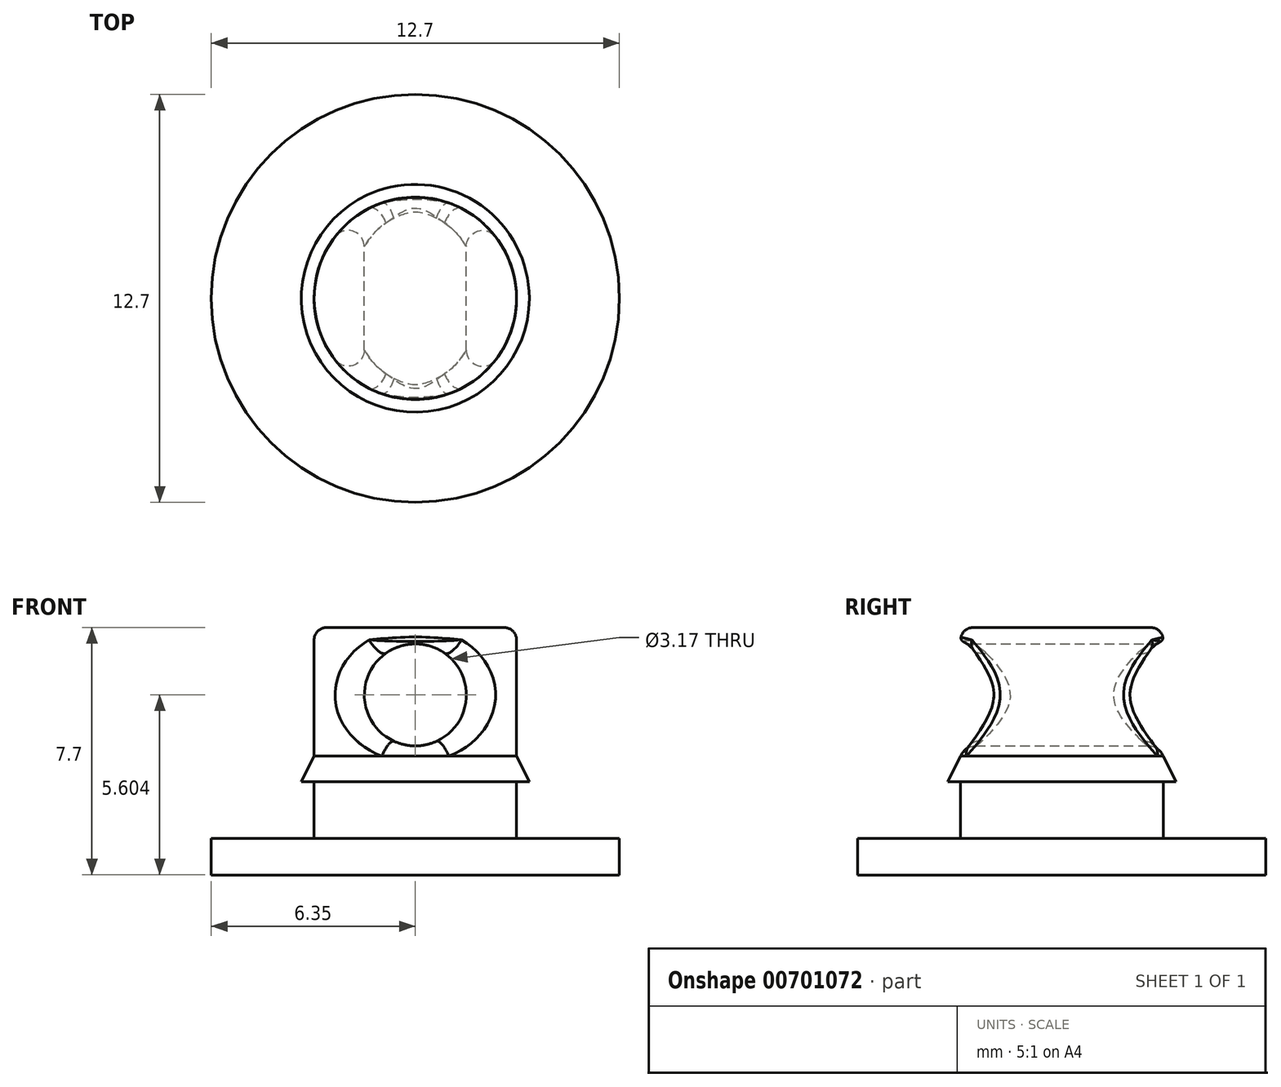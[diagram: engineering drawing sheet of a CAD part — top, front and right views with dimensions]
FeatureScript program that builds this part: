
annotation { "Feature Type Name" : "Feature", "Feature Type Description" : "" }
export const myFeature = defineFeature(function(context is Context, id is Id, definition is map)
    precondition{}
    {
        {
            var Q0;
            Q0=qCreatedBy(makeId("Top.planeOp"),FACE);
            var sketch = newSketch(context, id + "F0", { "sketchPlane" : qUnion([Q0])});
            skCircle(sketch, "E0", {"center": v(0, 0) * mm, "radius": 6.35 * mm});
            skSolve(sketch);
        }
        {
            var Q0;
            Q0=qCreatedBy(makeId("Top.planeOp"),FACE);
            var sketch = newSketch(context, id + "F1", { "sketchPlane" : qUnion([Q0])});
            skCircle(sketch, "E1", {"center": v(0, 0) * mm, "radius": 3.15 * mm});
            skSolve(sketch);
        }
        {
            var Q0;
            Q0 = qSketchRegion(id + "F0", true);
            extrude(context, id + "F2", {"entities" : qUnion([Q0]), "oppositeDirection" : true, "depth" : 1.14 * mm, "offsetDistance" : 25.4 * mm});
        }
        {
            var Q0;
            Q0 = qSketchRegion(id + "F1", true);
            extrude(context, id + "F3", {"entities" : qUnion([Q0]), "operationType" : NewBodyOperationType.ADD, "depth" : 1.77 * mm, "offsetDistance" : 25.4 * mm});
        }
        {
            var Q0;
            Q0=makeQuery(id+"F3.opExtrude","CAP_FACE",FACE,{"disambiguationData":[OSD([sQuery(id+"F1.wireOp",EDGE,"E1")])],"isStart":false});
            var sketch = newSketch(context, id + "F4", { "sketchPlane" : qUnion([Q0])});
            skCircle(sketch, "E2", {"center": v(0, 0) * mm, "radius": 3.55 * mm});
            skSolve(sketch);
        }
        {
            var Q0;
            Q0=makeQuery(id+"F4.imprint","IMPRINT",FACE,{"disambiguationData":[TD([[makeQuery(id+"F4.imprint","IMPRINT",EDGE,{"derivedFrom":makeQuery(id+"F3.opExtrude","CAP_EDGE",EDGE,{"disambiguationData":[OSD([sQuery(id+"F1.wireOp",EDGE,"E1")])],"isStart":false})}),1.0]])]});
            extrude(context, id + "F5", {"entities" : qUnion([Q0]), "operationType" : NewBodyOperationType.ADD, "depth" : 0.8 * mm, "offsetDistance" : 25.4 * mm});
        }
        {
            var Q1;
            Q1 = qSketchRegion(id + "F4", true);
            var Q2;
            Q2=makeQuery(id+"F5.opExtrude","CAP_FACE",FACE,{"disambiguationData":[OSD([sQuery(id+"F1.wireOp",EDGE,"E1")])],"isStart":false});
            loft(context, id + "F6", {"operationType" : NewBodyOperationType.ADD, "sheetProfilesArray" : [{ "sheetProfileEntities" : qUnion([Q1]) }, { "sheetProfileEntities" : qUnion([Q2]) }]});
        }
        {
            var Q0;
            Q0=makeQuery(id+"F5.opExtrude","CAP_FACE",FACE,{"disambiguationData":[OSD([sQuery(id+"F1.wireOp",EDGE,"E1")])],"isStart":false});
            var Q1;
            Q1 = qSketchRegion(id + "F8", true);
            extrude(context, id + "F7", {"entities" : qUnion([Q0, Q1]), "operationType" : NewBodyOperationType.ADD, "depth" : 4 * mm, "offsetDistance" : 25.4 * mm});
        }
        {
            var Q0;
            Q0=qCreatedBy(makeId("Front.planeOp"),FACE);
            var sketch = newSketch(context, id + "F8", { "sketchPlane" : qUnion([Q0])});
            skLineSegment(sketch, "E3", {"start": v(0, 0) * mm, "end": v(0, 2.56) * mm, "construction": true});
            skSolve(sketch);
        }
        {
            var Q0;
            Q0=qCreatedBy(makeId("Front.planeOp"),FACE);
            var sketch = newSketch(context, id + "F9", { "sketchPlane" : qUnion([Q0])});
            skLineSegment(sketch, "E4", {"start": v(0, 2.56) * mm, "end": v(0, 4.46) * mm, "construction": true});
            skSolve(sketch);
        }
        {
            var Q0;
            Q0=qCreatedBy(makeId("Front.planeOp"),FACE);
            var sketch = newSketch(context, id + "F10", { "sketchPlane" : qUnion([Q0])});
            skCircle(sketch, "E5", {"center": v(0, 4.46) * mm, "radius": 1.59 * mm});
            skSolve(sketch);
        }
        {
            var Q0;
            Q0 = qSketchRegion(id + "F10", true);
            extrude(context, id + "F11", {"entities" : qUnion([Q0]), "operationType" : NewBodyOperationType.REMOVE, "endBound" : BoundingType.THROUGH_ALL, "depth" : 25.4 * mm, "offsetDistance" : 25.4 * mm, "hasSecondDirection" : true, "secondDirectionBound" : SecondDirectionBoundingType.THROUGH_ALL, "secondDirectionOppositeDirection" : true, "secondDirectionDepth" : 25.4 * mm});
        }
        {
            var Q0;
            Q0=makeQuery(id+"F7.opExtrude","CAP_EDGE",EDGE,{"disambiguationData":[OSD([sQuery(id+"F1.wireOp",EDGE,"E1"),sQuery(id+"F4.wireOp",EDGE,"E2")])],"isStart":false});
            fillet(context, id + "F12", {"entities" : qUnion([Q0]), "radius" : 0.38 * mm, "tangentPropagation" : true, "allowEdgeOverflow" : false});
        }
        {
            var Q0;
            Q0=makeQuery(id+"F11.boolean.opBoolean","INTERSECT",EDGE,{"disambiguationData":[OD(1.0)],"derivedFrom":[makeQuery(id+"F7.opExtrude","SWEPT_FACE",FACE,{"disambiguationData":[OSD([sQuery(id+"F1.wireOp",EDGE,"E1"),sQuery(id+"F4.wireOp",EDGE,"E2")])]}),makeQuery(id+"F11.opExtrude","SWEPT_FACE",FACE,{"disambiguationData":[OSD([sQuery(id+"F10.wireOp",EDGE,"E5")])]})]});
            var Q1;
            Q1=makeQuery(id+"F11.boolean.opBoolean","INTERSECT",EDGE,{"disambiguationData":[OD(0.0)],"derivedFrom":[makeQuery(id+"F7.opExtrude","SWEPT_FACE",FACE,{"disambiguationData":[OSD([sQuery(id+"F1.wireOp",EDGE,"E1"),sQuery(id+"F4.wireOp",EDGE,"E2")])]}),makeQuery(id+"F11.opExtrude","SWEPT_FACE",FACE,{"disambiguationData":[OSD([sQuery(id+"F10.wireOp",EDGE,"E5")])]})]});
            fillet(context, id + "F13", {"entities" : qUnion([Q0, Q1]), "radius" : 0.5 * mm, "allowEdgeOverflow" : false});
        }
        {
            var Q0;
            {var subQ0=sQuery(id+"F4.wireOp",EDGE,"E2");var subQ1=sQuery(id+"F1.wireOp",EDGE,"E1");Q0=makeQuery(id+"F13.opFillet","BLEND_EDGE",EDGE,{"blendedFrom":[makeQuery(id+"F11.boolean.opBoolean","INTERSECT",EDGE,{"disambiguationData":[OD(1.0)],"derivedFrom":[makeQuery(id+"F7.opExtrude","SWEPT_FACE",FACE,{"disambiguationData":[OSD([subQ1,subQ0])]}),makeQuery(id+"F11.opExtrude","SWEPT_FACE",FACE,{"disambiguationData":[OSD([sQuery(id+"F10.wireOp",EDGE,"E5")])]})]}),makeQuery(id+"F12.opFillet","BLEND_FACE",FACE,{"disambiguationData":[OSD([subQ1,subQ0])]})],"blendedInto":[makeQuery(id+"F12.opFillet","BLEND_FACE",FACE,{"disambiguationData":[OSD([subQ1,subQ0])]})]});}
            var Q1;
            {var subQ0=sQuery(id+"F4.wireOp",EDGE,"E2");var subQ1=sQuery(id+"F1.wireOp",EDGE,"E1");Q1=makeQuery(id+"F13.opFillet","BLEND_EDGE",EDGE,{"blendedFrom":[makeQuery(id+"F11.boolean.opBoolean","INTERSECT",EDGE,{"disambiguationData":[OD(0.0)],"derivedFrom":[makeQuery(id+"F7.opExtrude","SWEPT_FACE",FACE,{"disambiguationData":[OSD([subQ1,subQ0])]}),makeQuery(id+"F11.opExtrude","SWEPT_FACE",FACE,{"disambiguationData":[OSD([sQuery(id+"F10.wireOp",EDGE,"E5")])]})]}),makeQuery(id+"F12.opFillet","BLEND_FACE",FACE,{"disambiguationData":[OSD([subQ1,subQ0])]})],"blendedInto":[makeQuery(id+"F12.opFillet","BLEND_FACE",FACE,{"disambiguationData":[OSD([subQ1,subQ0])]})]});}
            fillet(context, id + "F14", {"entities" : qUnion([Q0, Q1]), "radius" : 0.13 * mm, "tangentPropagation" : true, "allowEdgeOverflow" : false});
        }
    });
